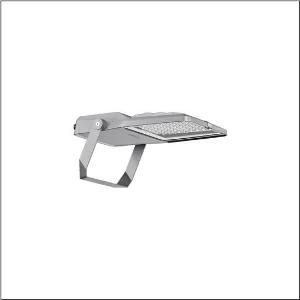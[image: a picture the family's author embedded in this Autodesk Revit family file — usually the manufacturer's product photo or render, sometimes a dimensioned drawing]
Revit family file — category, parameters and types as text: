
# Revit family: floodlight_fl_21_iq_mini___rs12_5xa7772b3b1a_fd5e
name_source: partatom
category: Lighting Fixtures
units: mm (PartAtom-declared; Revit-internal decimal feet)

## family parameters
Cut with Voids When Loaded = No
Host = Face
Light Source = No
Part Type = Normal
Room Calculation Point = No
Round Connector Dimension = Use Diameter
Shared = No

## types (1)
- --- (1 x LED, 5430 lm, 45.5 W, 3000K)
    Apparent Load = 46 VA
    CIE Flux Codes = 79 92 99 100 100
    Color Rendering = 80
    Color Temperature = 3000K
    Default Elevation = 1800 mm
    Description = Floodlight FL 21 iQ mini, floodlight, primary light control with lens, of PMMA, primary optical cover: protective disc, of toughened safety glass, transparent, light distribution: RS12, light emission: direct distribution, installation type: surface-mounted, lamps: LED, High Power LED, rated values: 5.430lm | 45,5W | 119,3lm/W (begin service life); end service life: 5.430lm | 48W; at 50% lumin. flux: 2.715lm | 21,4W | 126,9lm/W, colour temperature: 3000K, colour rendering: CRI > 80, light colour: 830, light setting 1 begin service life: 100% | 5.430lm | 45,5W | 119,3lm/W | 3.000K, light setting 1 end service life: 48W, further light settings possible, control: Street-Remote, Auto-Match, Temp-Guard, Night-Set, Smart-Wire, Desk-Remote (wireless, voltage-free reading and setting of iQ features in the workshop via application-optimized NFC function/RFID function), optimised constant luminous flux control (CLO 2.0), pre-setting: linear dimming characteristic, with terminal, 6-pole, mains connection: 220..240V, AC, 50/60Hz, luminaire housing, of diecast aluminium, powder-coated, SITECO metallic grey (DB 702S), corrosivity category C5 mid according to DIN EN ISO 12944suitable for swimming poolschlorine-resistant, sealing non-destructively replaceable, mounting bracket, of steel, galvanised, powder-coated, SITECO metallic grey (DB 702S), protection rating (complete): IP66, insulation class (complete): insulation class II (safety insulation), certification: CE, ENEC, VDE, protection symbol: D, impact resistance: IK08, permissible operating ambient temperature: -40..+40°C, permissible operating ambient temperature for outdoor applications: -40..+50°C, standard: DIN EN 12944, LABS conformity tested according to VDMA 24364:2018-05, packaging unit: 1 piece

Light Distribution: RS12
    Height = 70 mm
    Lamp = 1 x LED
    Lamp Light Flux = 5430 lm
    Lamp Power = 45.5 W
    Lamp count = 1
    Length = 485 mm
    Luminous efficacy = 119 lm/W
    Manufacturer = Siteco
    ModVariant = No
    Model = 5XA7772B3B1A
    Mounting Place = Pole
    Mounting Type = Pole annexe
    Number of Poles = 1
    OnlyDefault = Yes
    Power Factor = 1
    Product Name = Floodlight FL 21 iQ mini | RS12
    Product group = floodlight | pylon annexe
    ProductGroupID = 6201
    Protection Class = Protection class II
    Protection Degree = IP 66
    RLX_Detail_Level = 1
    RLX_Emergency_Light_Flux = 0 lm
    RLX_Emergency_Type = 0
    RLX_Emergency_Type_DB = No
    RlxData = <blob elided: 91029 chars, md5=11672313>
    Socket = socket
    Standby Power = 0 W
    System Light Flux = 5430 lm
    System Power = 46 W
    Type Comments = factory setting: luminous flux: 100 % | dim-lin: 254 | 463 mA
    Type Image = l_1006845.jpg
    URL = http://relux.com
    VarID = @adj_168885
    Voltage = 0 V
    Weight = 0.00 kg
    Width = 337 mm

## geometry (parser evidence)
native form markers: Blend x4, Sweep x13
no freeform markers — native parametric forms only
